# Revit family: Accessory-Flush_Actuator_Plate-KOHLER-Note-K-75891IN
name_source: partatom
category: Specialty Equipment
revit_build: Autodesk Revit 2017 (Build: 20160225_1515(x64)
units: mm (PartAtom-declared; Revit-internal decimal feet)

## family parameters
Cut with Voids When Loaded = No
Host = Face
OmniClass Number = 23.31.25.00
Part Type = Normal
Room Calculation Point = No
Round Connector Dimension = Use Diameter
Shared = No

## types (3) — shared parameters
ADA Compliant = No
Assembly Code = C1030200
Date Modified = 01/05/2021
Default Elevation = 42"
Description = Face Plate for Inwall Tank
Height = 6 3/8"
Length = 7/16"
Manufacturer = KOHLER Co.
Master Format 2014 = 10 28 00
Master Format 2014 Name = Toilet, Bath, and Laundry Accessories
Material = Plastic
Product Documentation Link = http://resources.kohler.com
Product Name = Note
URL = https://www.kohler.co.in
WaterSense Certified = No
Width = 8 7/8"

## per-type parameters (varying)
| type | Finish | Model | Product Page URL | Type |
| CP- Polished Chrome | KOHLER-Plastic-CP-Polished_Chrome | K-75891IN-M-CP |  | 1 |
| 0- Glossy White | Kohler-Plastic-0-White | K-75891IN-M-0 | https://www.kohler.co.in | 3 |
| 7-Glossy Black | Kohler-Plastic-7-Black_Black | K-75891IN-M-7 | https://www.kohler.co.in | 2 |

## geometry (parser evidence)
native form markers: Sweep x6
no freeform markers — native parametric forms only
